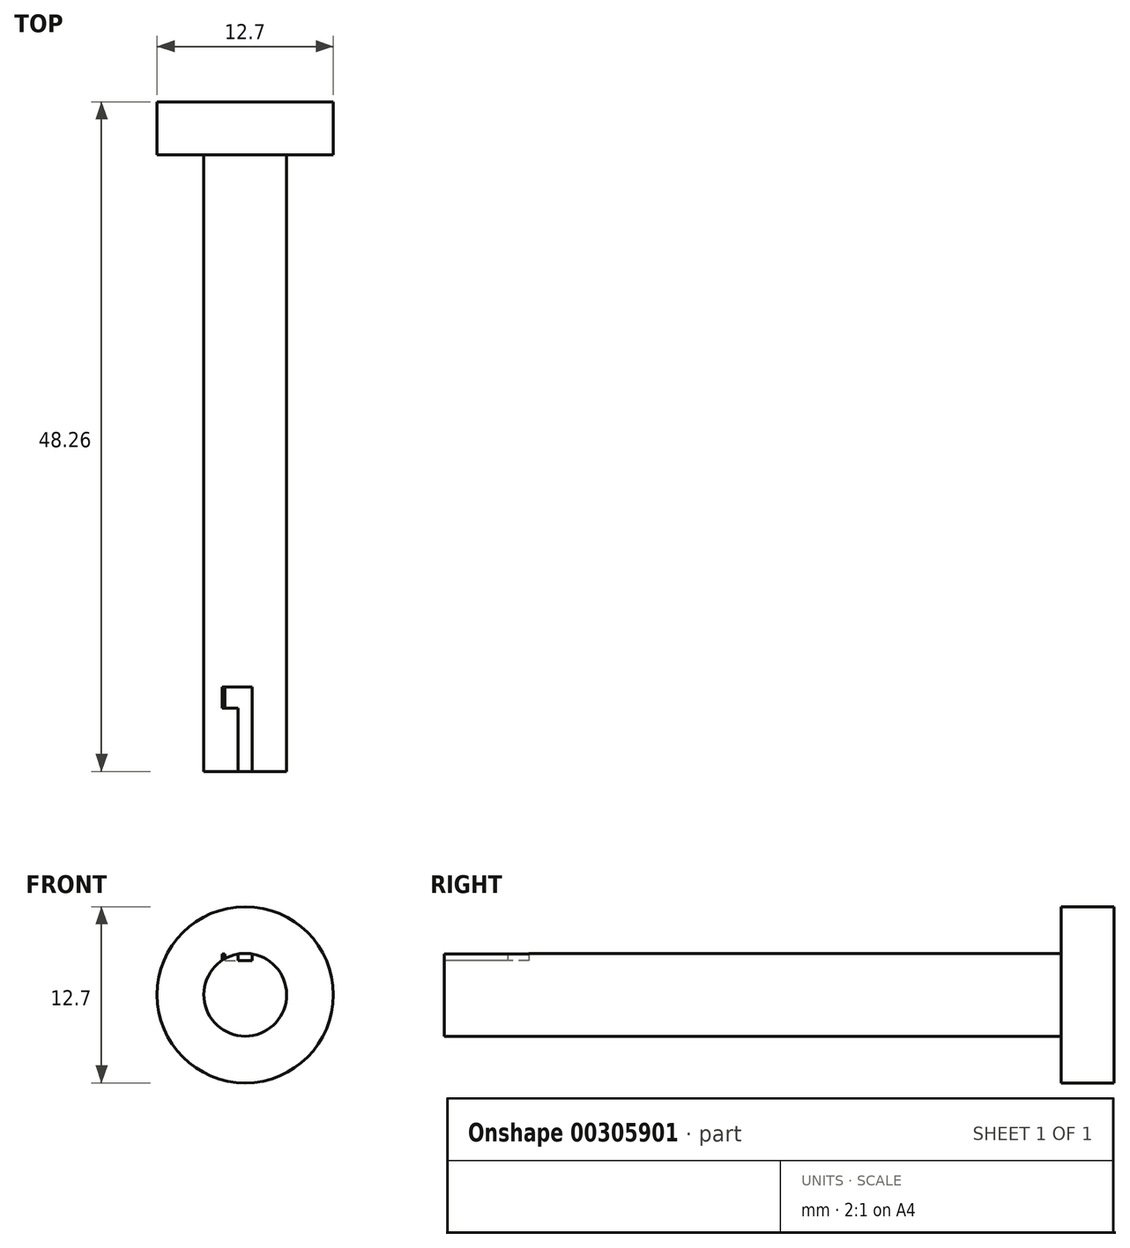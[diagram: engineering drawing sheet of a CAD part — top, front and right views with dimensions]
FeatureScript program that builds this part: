
annotation { "Feature Type Name" : "Feature", "Feature Type Description" : "" }
export const myFeature = defineFeature(function(context is Context, id is Id, definition is map)
    precondition{}
    {
        {
            var Q0;
            Q0=qCreatedBy(makeId("Front.planeOp"),FACE);
            var sketch = newSketch(context, id + "F0", { "sketchPlane" : qUnion([Q0])});
            skCircle(sketch, "E0", {"center": v(0, 0) * mm, "radius": 2.98 * mm});
            skSolve(sketch);
        }
        {
            var Q0;
            Q0 = qSketchRegion(id + "F0", true);
            extrude(context, id + "F1", {"entities" : qUnion([Q0]), "depth" : 44.45 * mm});
        }
        {
            var Q0;
            Q0=makeQuery(id+"F1.opExtrude","CAP_FACE",FACE,{"disambiguationData":[OSD([sQuery(id+"F0.wireOp",EDGE,"E0")])],"isStart":false});
            var sketch = newSketch(context, id + "F2", { "sketchPlane" : qUnion([Q0])});
            skCircle(sketch, "E1", {"center": v(0, 0) * mm, "radius": 6.35 * mm});
            skSolve(sketch);
        }
        {
            var Q0;
            Q0=makeQuery(id+"F1.opExtrude","CAP_FACE",FACE,{"disambiguationData":[OSD([sQuery(id+"F0.wireOp",EDGE,"E0")])],"isStart":true});
            var sketch = newSketch(context, id + "F3", { "sketchPlane" : qUnion([Q0])});
            skCircle(sketch, "E2", {"center": v(0, 0) * mm, "radius": 6.35 * mm});
            skSolve(sketch);
        }
        {
            var Q0;
            Q0 = qSketchRegion(id + "F3", true);
            extrude(context, id + "F4", {"entities" : qUnion([Q0]), "operationType" : NewBodyOperationType.ADD, "depth" : 3.8 * mm});
        }
        {
            var Q0;
            Q0=makeQuery(id+"F2.imprint","IMPRINT",FACE,{"disambiguationData":[TD([[makeQuery(id+"F2.imprint","IMPRINT",EDGE,{"derivedFrom":makeQuery(id+"F1.opExtrude","CAP_EDGE",EDGE,{"disambiguationData":[OSD([sQuery(id+"F0.wireOp",EDGE,"E0")])],"isStart":false})}),1.0]])]});
            var sketch = newSketch(context, id + "F5", { "sketchPlane" : qUnion([Q0])});
            skPoint(sketch, "E3.middle", {"position": v(0, 2.89) * mm});
            skLineSegment(sketch, "E4.bottom", {"start": v(-0.5, 3.5) * mm, "end": v(0.5, 3.5) * mm});
            skLineSegment(sketch, "E4.top", {"start": v(-0.5, 2.48) * mm, "end": v(0.5, 2.48) * mm});
            skLineSegment(sketch, "E4.left", {"start": v(-0.5, 3.5) * mm, "end": v(-0.5, 2.48) * mm});
            skLineSegment(sketch, "E4.right", {"start": v(0.5, 3.5) * mm, "end": v(0.5, 2.48) * mm});
            skPoint(sketch, "E4.middle", {"position": v(0, 2.98) * mm});
            skSolve(sketch);
        }
        {
            var Q0;
            Q0 = qSketchRegion(id + "F5", true);
            extrude(context, id + "F6", {"entities" : qUnion([Q0]), "operationType" : NewBodyOperationType.REMOVE, "oppositeDirection" : true, "depth" : 25.4 * mm});
        }
        {
            var Q0;
            Q0=makeQuery(id+"F6.boolean.opBoolean","COPY",FACE,{"derivedFrom":makeQuery(id+"F6.opExtrude","SWEPT_FACE",FACE,{"disambiguationData":[OSD([sQuery(id+"F5.wireOp",EDGE,"E4.left")])]})});
            var sketch = newSketch(context, id + "F7", { "sketchPlane" : qUnion([Q0])});
            skLineSegment(sketch, "E5", {"start": v(-44.45, 2.7) * mm, "end": v(-39.12, 2.7) * mm});
            skLineSegment(sketch, "E6.bottom", {"start": v(-39.88, 2.94) * mm, "end": v(-38.35, 2.94) * mm});
            skLineSegment(sketch, "E6.top", {"start": v(-39.88, 2.48) * mm, "end": v(-38.35, 2.48) * mm});
            skLineSegment(sketch, "E6.left", {"start": v(-39.88, 2.94) * mm, "end": v(-39.88, 2.48) * mm});
            skLineSegment(sketch, "E6.right", {"start": v(-38.35, 2.94) * mm, "end": v(-38.35, 2.48) * mm});
            skPoint(sketch, "E6.middle", {"position": v(-39.12, 2.7) * mm});
            skSolve(sketch);
        }
        {
            var Q0;
            {var subQ4=sQuery(id+"F7.wireOp",EDGE,"E6.bottom");Q0=makeQuery(id+"F7.imprint","IMPRINT",FACE,{"disambiguationData":[TD([[makeQuery(id+"F7.imprint","IMPRINT",EDGE,{"derivedFrom":subQ4}),-1.0]])]});}
            extrude(context, id + "F8", {"entities" : qUnion([Q0]), "operationType" : NewBodyOperationType.REMOVE, "oppositeDirection" : true, "depth" : 1.52 * mm});
        }
        {
            var Q0;
            Q0=makeQuery(id+"F8.boolean.opBoolean","MERGE",FACE,{"derivedFrom":[makeQuery(id+"F6.boolean.opBoolean","COPY",FACE,{"derivedFrom":makeQuery(id+"F6.opExtrude","SWEPT_FACE",FACE,{"disambiguationData":[OSD([sQuery(id+"F5.wireOp",EDGE,"E4.top")])]})}),makeQuery(id+"F8.opExtrude","SWEPT_FACE",FACE,{"disambiguationData":[OSD([sQuery(id+"F7.wireOp",EDGE,"E6.top")])]})]});
            var sketch = newSketch(context, id + "F9", { "sketchPlane" : qUnion([Q0])});
            skLineSegment(sketch, "E7.bottom", {"start": v(-1.67, -38.35) * mm, "end": v(-1.46, -38.35) * mm});
            skLineSegment(sketch, "E7.top", {"start": v(-1.67, -39.88) * mm, "end": v(-1.46, -39.88) * mm});
            skLineSegment(sketch, "E7.left", {"start": v(-1.67, -38.35) * mm, "end": v(-1.67, -39.88) * mm});
            skLineSegment(sketch, "E7.right", {"start": v(-1.46, -38.35) * mm, "end": v(-1.46, -39.88) * mm});
            skSolve(sketch);
        }
        {
            var Q0;
            Q0=makeQuery(id+"F9.imprint","IMPRINT",FACE,{"disambiguationData":[TD([[makeQuery(id+"F9.imprint","IMPRINT",EDGE,{"derivedFrom":sQuery(id+"F9.wireOp",EDGE,"E7.bottom")}),-1.0]])]});
            extrude(context, id + "F10", {"entities" : qUnion([Q0]), "operationType" : NewBodyOperationType.ADD, "depth" : 0.46 * mm});
        }
        {
            var Q0;
            Q0=makeQuery(id+"F6.boolean.opBoolean","COPY",FACE,{"derivedFrom":makeQuery(id+"F6.opExtrude","CAP_FACE",FACE,{"disambiguationData":[OSD([sQuery(id+"F5.wireOp",EDGE,"E4.bottom"),sQuery(id+"F5.wireOp",EDGE,"E4.top"),sQuery(id+"F5.wireOp",EDGE,"E4.left"),sQuery(id+"F5.wireOp",EDGE,"E4.right")])],"isStart":false})});
            extrude(context, id + "F11", {"entities" : qUnion([Q0]), "operationType" : NewBodyOperationType.ADD, "depth" : 19.3 * mm});
        }
    });
